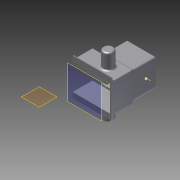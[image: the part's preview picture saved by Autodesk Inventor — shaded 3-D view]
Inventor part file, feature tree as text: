
AUTODESK INVENTOR PART (.ipt)
format: ipt  version: 2012 (Build 160160000, 160)  size: 953,344 bytes
history: native  units: mm
features: sketch x34, extrude x34, reference x30, projected_geometry x24, fillet x13, plane x5, other x2
ambient origin geometry x8: Origin, YZ Plane, XZ Plane, XY Plane, X Axis, Y Axis, Z Axis, Center Point
bodies: Solid1 (feature_tree)
feature tree (142):
  plane  "Work Plane2"
  sketch  "Sketch3"  dims[d1=0.3mm d2=0.3mm]
  plane  "Work Plane3"
  extrude  "Extrusion1"  Depth=0.3mm
  extrude  "Extrusion2"  Depth=10.0mm TaperAngle=0.0deg
  plane  "Work Plane4"
  extrude  "Extrusion3"  Depth=10.0mm TaperAngle=0.0deg
  extrude  "Extrusion4"  Depth=2.0mm
  extrude  "Extrusion5"  Depth=2.0mm
  extrude  "Extrusion6"  Depth=2.0mm TaperAngle=0.0deg
  extrude  "Extrusion7"  TaperAngle=0.0deg  [1 undecoded]
  extrude  "Extrusion8"  TaperAngle=0.0deg  [1 undecoded]
  fillet  "Fillet3"  Radius=20.0mm
  fillet  "Fillet4"  Radius=20.0mm
  fillet  "Fillet5"  Radius=0.3mm
  extrude  "Extrusion10"  Depth=0.3mm
  extrude  "Extrusion11"  Depth=0.3mm TaperAngle=0.0deg
  extrude  "Extrusion12"  Depth=1.0mm
  extrude  "Extrusion13"  Depth=2.0mm TaperAngle=0.0deg
  extrude  "Extrusion14"  Depth=0.3mm
  extrude  "Extrusion15"  Depth=0.3mm
  extrude  "Extrusion16"  TaperAngle=0.0deg  [1 undecoded]
  extrude  "Extrusion17"  Depth=2.0mm
  extrude  "Extrusion18"  Depth=2.0mm TaperAngle=0.0deg
  extrude  "Extrusion20"  Depth=14.0mm
  extrude  "Extrusion21"  Depth=7.0mm TaperAngle=0.0deg
  plane  "Work Plane5"
  extrude  "Extrusion22"  Depth=3.3mm
  extrude  "Extrusion23"  Depth=3.3mm
  extrude  "Extrusion24"  Depth=0.3mm
  extrude  "Extrusion25"  Depth=0.3mm
  plane  "Work Plane7"
  extrude  "Extrusion26"  Depth=20.0mm TaperAngle=0.0deg
  extrude  "Extrusion27"  Depth=0.3mm
  extrude  "Extrusion28"  Depth=0.3mm
  extrude  "Extrusion29"  Depth=2.0mm
  extrude  "Extrusion30"  Depth=2.0mm
  extrude  "Extrusion31"  TaperAngle=45.0deg  [1 undecoded]
  extrude  "Extrusion34"  Depth=9.0mm
  other  "Work Axis1"
  fillet  "Fillet47"  Radius=10.0mm
  fillet  "Fillet48"  [1 undecoded]
  fillet  "Fillet49"  Radius=10.0mm
  fillet  "Fillet50"  Radius=10.0mm
  fillet  "Fillet51"  Radius=10.0mm
  fillet  "Fillet52"  Radius=0.3mm
  fillet  "Fillet54"  Radius=0.3mm
  fillet  "Fillet55"  Radius=10.0mm
  other  "Work Axis3"
  extrude  "Extrusion35"  Depth=10.0mm TaperAngle=0.0deg
  extrude  "Extrusion36"  Depth=10.0mm TaperAngle=0.0deg
  extrude  "Extrusion37"  Depth=25.4mm TaperAngle=0.0deg
  extrude  "Extrusion38"  Depth=2.0mm
  fillet  "Fillet56"  Radius=2.0mm
  fillet  "Fillet57"  Radius=2.0mm
  reference  "Reference32"
  sketch  "Sketch4"  dims[d3=2.0mm d4=10.0mm d5=0.0mm]
  reference  "Reference33"
  sketch  "Sketch5"  dims[d6=0.3mm d7=10.0mm d8=0.0mm]
  sketch  "Sketch7"  dims[d9=2.0mm d10=2.0mm]
  projected_geometry  "Projected Loop3"
  sketch  "Sketch8"  dims[d11=2.0mm d12=2.0mm]
  sketch  "Sketch10"  dims[d13=120.0mm d14=2.0mm d15=0.0mm]
  reference  "Reference36"
  sketch  "Sketch11"  dims[d24=2.0mm d25=0.0mm]
  reference  "Reference37"
  sketch  "Sketch12"  dims[d26=2.0mm d27=0.0mm d28=20.0mm d29=0.0mm d31=20.0mm d32=0.0mm d34=0.3mm]
  sketch  "Sketch15"  dims[d35=20.0mm d36=0.0mm d37=0.3mm]
  projected_geometry  "Projected Loop5"
  projected_geometry  "Projected Loop6"
  sketch  "Sketch16"  dims[d38=10.0mm d39=0.0mm d40=0.3mm d41=0.0mm]
  reference  "Reference46"
  reference  "Reference47"
  reference  "Reference48"
  reference  "Reference49"
  reference  "Reference50"
  reference  "Reference51"
  reference  "Reference52"
  reference  "Reference53"
  sketch  "Sketch17"  dims[d43=1.0mm d44=1.0mm]
  reference  "Reference54"
  reference  "Reference55"
  reference  "Reference56"
  reference  "Reference57"
  reference  "Reference58"
  reference  "Reference59"
  reference  "Reference60"
  reference  "Reference61"
  sketch  "Sketch18"  dims[d45=1.0mm d52=2.0mm d53=0.0mm]
  reference  "Reference62"
  sketch  "Sketch19"  dims[d58=2.0mm d59=0.0mm d60=0.3mm]
  projected_geometry  "Projected Loop7"
  projected_geometry  "Projected Loop8"
  sketch  "Sketch20"  dims[d61=0.3mm d62=0.3mm]
  projected_geometry  "Projected Loop9"
  projected_geometry  "Projected Loop10"
  sketch  "Sketch21"  dims[d63=0.3mm d64=0.0mm]
  projected_geometry  "Projected Loop11"
  sketch  "Sketch22"  dims[d66=0.0mm d67=2.0mm]
  reference  "Reference63"
  reference  "Reference64"
  reference  "Reference65"
  reference  "Reference66"
  reference  "Reference67"
  reference  "Reference68"
  reference  "Reference69"
  reference  "Reference70"
  sketch  "Sketch23"  dims[d68=2.0mm d69=2.0mm d70=0.0mm]
  projected_geometry  "Projected Loop12"
  projected_geometry  "Projected Loop13"
  projected_geometry  "Projected Loop14"
  projected_geometry  "Projected Loop15"
  sketch  "Sketch25"  dims[d72=2.0mm d73=0.0mm d74=14.0mm]
  projected_geometry  "Projected Loop16"
  sketch  "Sketch26"  dims[d78=2.0mm d79=0.0mm d80=7.0mm d81=0.0mm]
  sketch  "Sketch28"  dims[d82=10.0mm d83=0.0mm d84=3.3mm]
  projected_geometry  "Projected Loop21"
  sketch  "Sketch29"  dims[d85=3.3mm d86=3.3mm]
  projected_geometry  "Projected Loop22"
  projected_geometry  "Projected Loop23"
  sketch  "Sketch30"  dims[d87=3.3mm d88=0.3mm]
  projected_geometry  "Projected Loop24"
  sketch  "Sketch31"  dims[d89=0.3mm d90=0.3mm]
  projected_geometry  "Projected Loop25"
  sketch  "Sketch32"  dims[d91=0.3mm d94=20.0mm d95=0.0mm]
  sketch  "Sketch33"  dims[d97=0.3mm d98=0.3mm]
  projected_geometry  "Projected Loop26"
  sketch  "Sketch34"  dims[d99=0.3mm d100=0.3mm]
  projected_geometry  "Projected Loop27"
  sketch  "Sketch35"  dims[d101=0.3mm d102=0.0mm d103=2.0mm]
  projected_geometry  "Projected Loop28"
  projected_geometry  "Projected Loop29"
  sketch  "Sketch37"  dims[d104=2.0mm d105=2.0mm]
  sketch  "Sketch38"  dims[d106=2.0mm d111=45.0deg]
  projected_geometry  "Projected Loop31"
  sketch  "Sketch41"  dims[d112=9.0mm d113=9.0mm d114=10.0mm d115=0.0mm d116=0.0mm d117=0.0mm d123=10.0mm d124=0.0mm d132=10.0mm d133=0.0mm d134=10.0mm d135=0.0mm d138=0.3mm d139=0.0mm d151=0.3mm d152=0.0mm d153=10.0mm d154=0.0mm]
  reference  "Reference73"
  sketch  "Sketch42"  dims[d155=10.0mm d156=0.0mm d157=10.0mm d158=0.0mm]
  sketch  "Sketch43"  dims[d159=4.0mm d160=10.0mm d161=0.0mm]
  projected_geometry  "Projected Loop33"
  sketch  "Sketch44"  dims[d162=10.0mm d163=0.0mm d186=25.4mm d187=0.0mm]
  sketch  "Sketch45"  dims[d189=1.0mm d190=2.0mm d191=2.0mm d192=2.0mm d193=2.0mm d194=1.0mm d196=2.0mm d197=1.5mm d198=108.5mm d199=0.0mm d200=1.657mm d201=0.0mm d202=35.343104mm d203=17.671552mm d204=21.697757mm d205=10.848879mm d206=12.7mm d207=19.05mm d208=0.0mm d209=19.05mm d210=0.0mm d211=2.0mm d212=2.0mm]
note: 5 required parameter values undecoded (feature->parameter linkage not recoverable at this tier; creation-order binding heuristic only, values carry confidence <= 0.55)
